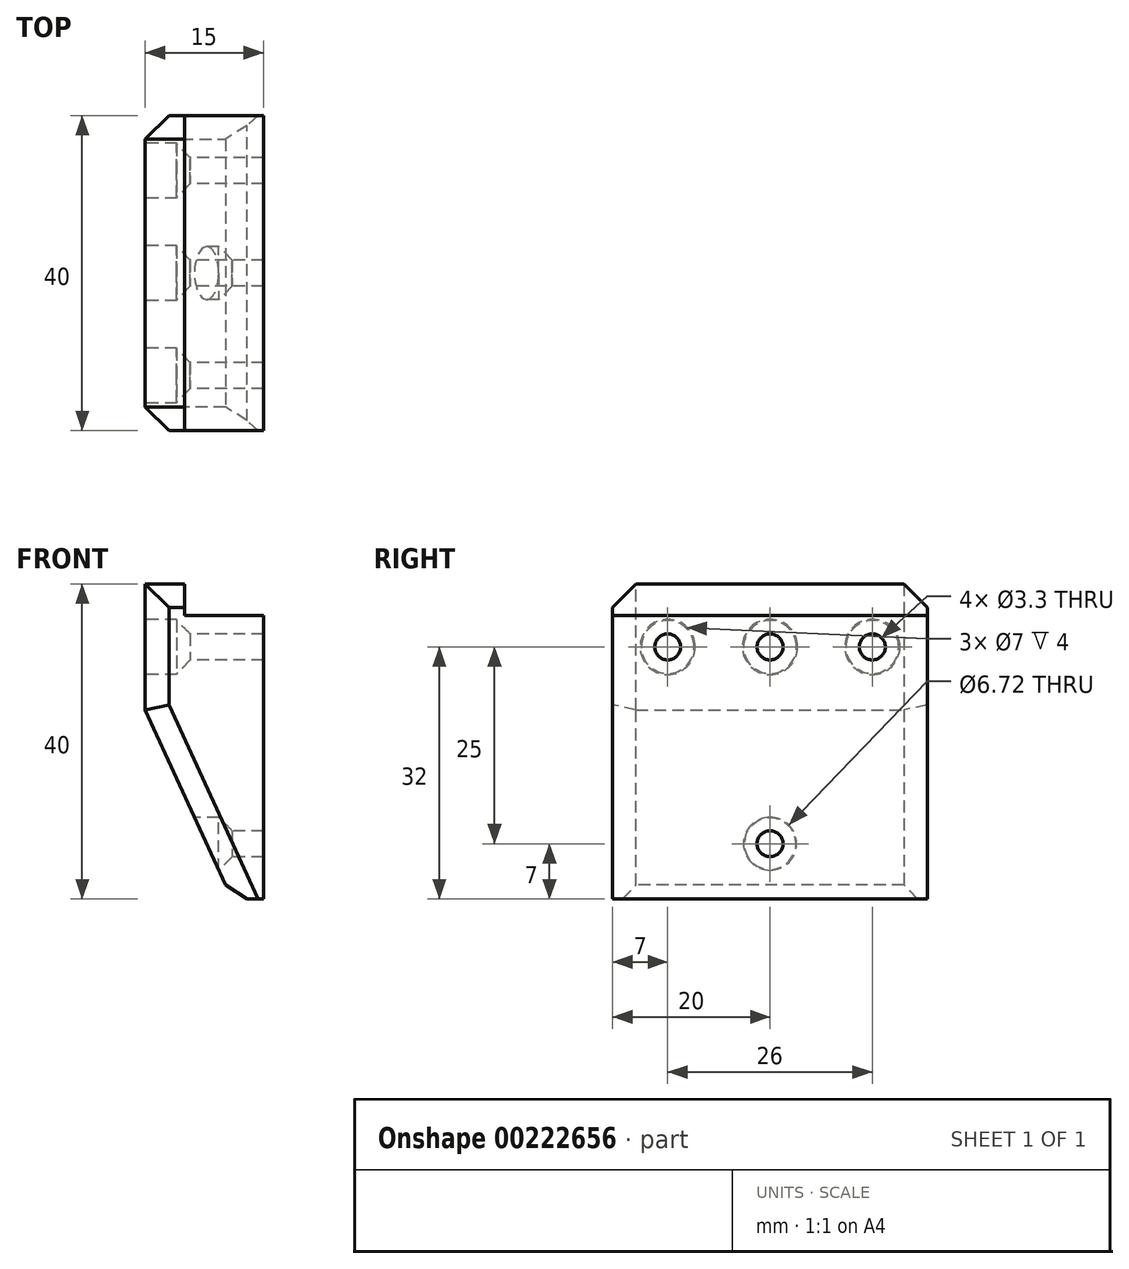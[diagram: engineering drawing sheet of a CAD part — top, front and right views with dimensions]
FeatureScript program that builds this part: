
annotation { "Feature Type Name" : "Feature", "Feature Type Description" : "" }
export const myFeature = defineFeature(function(context is Context, id is Id, definition is map)
    precondition{}
    {
        {
            var Q0;
            Q0=qCreatedBy(makeId("Front.planeOp"),FACE);
            var sketch = newSketch(context, id + "F0", { "sketchPlane" : qUnion([Q0])});
            skLineSegment(sketch, "E0", {"start": v(0, 0) * mm, "end": v(-15, 0) * mm});
            skLineSegment(sketch, "E1", {"start": v(-15, 0) * mm, "end": v(-15, -16) * mm});
            skLineSegment(sketch, "E2", {"start": v(-15, -16) * mm, "end": v(-4, -40) * mm});
            skLineSegment(sketch, "E3", {"start": v(-4, -40) * mm, "end": v(0, -40) * mm});
            skLineSegment(sketch, "E4", {"start": v(0, -40) * mm, "end": v(0, 0) * mm});
            skSolve(sketch);
        }
        {
            var Q0;
            Q0=makeQuery(id+"F0.imprint","IMPRINT",FACE,{"disambiguationData":[TD([[makeQuery(id+"F0.imprint","IMPRINT",EDGE,{"derivedFrom":sQuery(id+"F0.wireOp",EDGE,"E0")}),1.0]])]});
            extrude(context, id + "F1", {"entities" : qUnion([Q0]), "endBound" : BoundingType.SYMMETRIC, "depth" : 40 * mm});
        }
        {
            var Q0;
            Q0=makeQuery(id+"F1.opExtrude","SWEPT_FACE",FACE,{"disambiguationData":[OSD([sQuery(id+"F0.wireOp",EDGE,"E1")])]});
            var sketch = newSketch(context, id + "F2", { "sketchPlane" : qUnion([Q0])});
            skLineSegment(sketch, "E5.0", {"start": v(20, 0) * mm, "end": v(-20, 0) * mm, "construction": true});
            skCircle(sketch, "E6", {"center": v(0, -8) * mm, "radius": 3.5 * mm});
            skCircle(sketch, "E7", {"center": v(0, -33) * mm, "radius": 3.5 * mm});
            skCircle(sketch, "E8", {"center": v(-13, -8) * mm, "radius": 3.5 * mm});
            skCircle(sketch, "E9", {"center": v(13, -8) * mm, "radius": 3.5 * mm});
            skSolve(sketch);
        }
        {
            var Q0;
            Q0 = qSketchRegion(id + "F2", true);
            extrude(context, id + "F3", {"entities" : qUnion([Q0]), "operationType" : NewBodyOperationType.REMOVE, "oppositeDirection" : true, "depth" : 4 * mm});
        }
        {
            var Q0;
            Q0=sQuery(id+"F2.wireOp",VERTEX,"E7.center");
            var Q1;
            Q1=sQuery(id+"F2.wireOp",VERTEX,"E6.center");
            var Q2;
            Q2=sQuery(id+"F2.wireOp",VERTEX,"E8.center");
            var Q3;
            Q3=sQuery(id+"F2.wireOp",VERTEX,"E9.center");
            var Q4;
            Q4=makeQuery(id+"F1.opExtrude","SWEPT_BODY",BODY,{"disambiguationData":[OSD([sQuery(id+"F0.wireOp",EDGE,"E0"),sQuery(id+"F0.wireOp",EDGE,"E1"),sQuery(id+"F0.wireOp",EDGE,"E2"),sQuery(id+"F0.wireOp",EDGE,"E3"),sQuery(id+"F0.wireOp",EDGE,"E4")])]});
            hole(context, id + "F4", {"style" : HoleStyle.C_SINK, "endStyle" : HoleEndStyle.THROUGH, "standardTappedOrClearance" : lookupTablePath({ "standard" : "ISO", "fit" : "Normal", "size" : "M3", "type" : "Clearance" }), "standardBlindInLast" : lookupTablePath({ "fit" : "Standard", "standard" : "ISO", "size" : "M3", "type" : "Clearance" }), "holeDiameter" : 3.3 * mm, "cSinkDiameter" : 6.72 * mm, "cSinkAngle" : 90 * degree, "locations" : qUnion([Q0, Q1, Q2, Q3]), "scope" : qUnion([Q4]), "isTappedThrough" : true});
        }
        {
            var Q0;
            Q0=makeQuery(id+"F1.opExtrude","CAP_EDGE",EDGE,{"disambiguationData":[OSD([sQuery(id+"F0.wireOp",EDGE,"E0")])],"isStart":false});
            var Q1;
            Q1=makeQuery(id+"F1.opExtrude","CAP_EDGE",EDGE,{"disambiguationData":[OSD([sQuery(id+"F0.wireOp",EDGE,"E0")])],"isStart":true});
            var Q2;
            Q2=makeQuery(id+"F1.opExtrude","CAP_EDGE",EDGE,{"disambiguationData":[OSD([sQuery(id+"F0.wireOp",EDGE,"E1")])],"isStart":true});
            var Q3;
            Q3=makeQuery(id+"F1.opExtrude","CAP_EDGE",EDGE,{"disambiguationData":[OSD([sQuery(id+"F0.wireOp",EDGE,"E1")])],"isStart":false});
            var Q4;
            Q4=makeQuery(id+"F1.opExtrude","CAP_EDGE",EDGE,{"disambiguationData":[OSD([sQuery(id+"F0.wireOp",EDGE,"E2")])],"isStart":false});
            var Q5;
            Q5=makeQuery(id+"F1.opExtrude","CAP_EDGE",EDGE,{"disambiguationData":[OSD([sQuery(id+"F0.wireOp",EDGE,"E2")])],"isStart":true});
            var Q6;
            Q6=makeQuery(id+"F1.opExtrude","SWEPT_EDGE",EDGE,{"disambiguationData":[OSD([sQuery(id+"F0.wireOp",EDGE,"E2"),sQuery(id+"F0.wireOp",EDGE,"E3")])]});
            chamfer(context, id + "F5", {"entities" : qUnion([Q0, Q1, Q2, Q3, Q4, Q5, Q6]), "width" : 3 * mm, "tangentPropagation" : true});
        }
        {
            var Q0;
            Q0=qCreatedBy(makeId("Front.planeOp"),FACE);
            var sketch = newSketch(context, id + "F6", { "sketchPlane" : qUnion([Q0])});
            skLineSegment(sketch, "E10.bottom", {"start": v(0, -4) * mm, "end": v(-10, -4) * mm});
            skLineSegment(sketch, "E10.top", {"start": v(0, 0) * mm, "end": v(-10, 0) * mm});
            skLineSegment(sketch, "E10.left", {"start": v(0, -4) * mm, "end": v(0, 0) * mm});
            skLineSegment(sketch, "E10.right", {"start": v(-10, -4) * mm, "end": v(-10, 0) * mm});
            skSolve(sketch);
        }
        {
            var Q0;
            Q0 = qSketchRegion(id + "F6", true);
            extrude(context, id + "F7", {"entities" : qUnion([Q0]), "operationType" : NewBodyOperationType.REMOVE, "endBound" : BoundingType.THROUGH_ALL, "oppositeDirection" : true, "depth" : 25 * mm, "hasSecondDirection" : true, "secondDirectionBound" : SecondDirectionBoundingType.THROUGH_ALL, "secondDirectionOppositeDirection" : false, "secondDirectionDepth" : 25 * mm});
        }
    });
